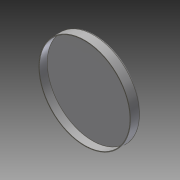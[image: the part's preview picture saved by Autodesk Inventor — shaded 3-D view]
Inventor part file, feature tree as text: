
AUTODESK INVENTOR PART (.ipt)
format: ipt  version: 2014 SP1 (Build 180222100, 222)  size: 286,720 bytes
history: native  units: in
note: dims shown in document units (in); Inventor stores cm internally (conversion verified against a paired STEP export)
features: other x2, extrude x1, fillet x1, imported_body x1, sketch x1
ambient origin geometry x8: Origin, YZ Plane, XZ Plane, XY Plane, X Axis, Y Axis, Z Axis, Center Point
bodies: Body1 (feature_tree)
feature tree (6):
  other  "Boss-Extrude2"
  other  "AM-2235 gear cap1"
  extrude  "Extrusion1"  Depth=0.05in
  fillet  "Fillet1"  Radius=0.75in
  imported_body  "Base1"
  sketch  "Sketch1"  dims[d0=2.575in d1=0.7688in d2=0.75in d3=0.1in d4=2.3622in d6=360.0deg d8=0.25in d9=0.05in d10=0.0in d11=0.05in]
